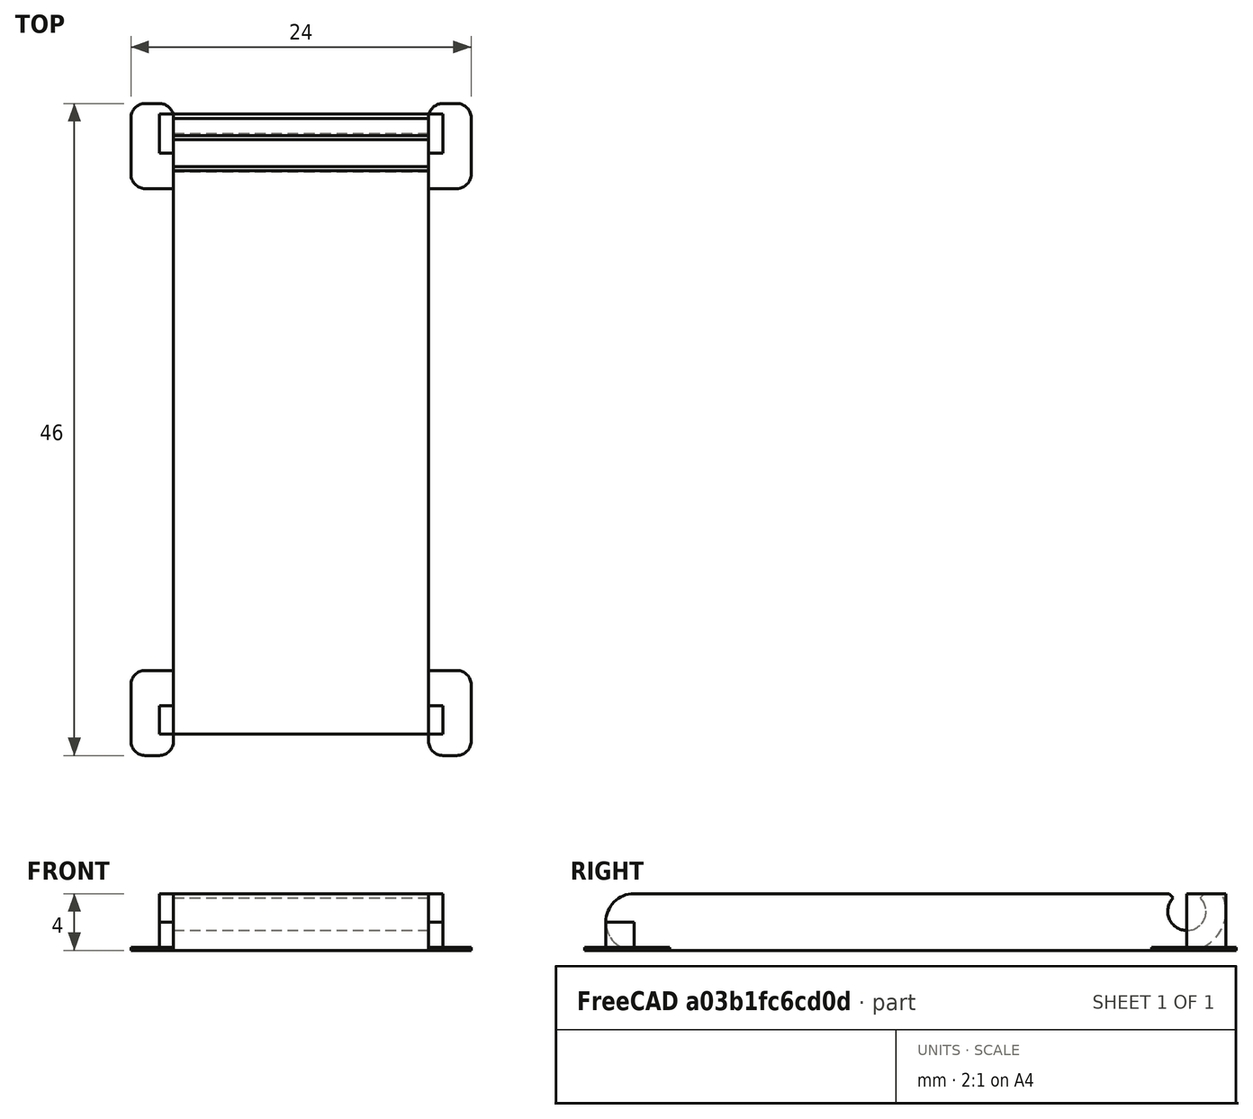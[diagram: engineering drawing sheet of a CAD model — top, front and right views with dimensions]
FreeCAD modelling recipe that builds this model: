
FCSTD DOCUMENT  (FreeCAD 0.14R3700 (Git))
Label: Phone_stand_flippable_backplate
License: CC-BY 3.0
LicenseURL: http://creativecommons.org/licenses/by/3.0/
objects: Sketcher::SketchObject×4, PartDesign::Pad×4, Mesh::Feature×1
note: 12 computed .brp shape members not serialized (recipe doc carries the construction recipe); baked Part::Feature solids carry a one-line shape summary decoded from their .brp

FEATURE [Sketcher::SketchObject] Sketch  label="X-Section"
  Placement = pos=(0,0,0) rot=(0.57735,0.57735,0.57735;2.0944rad)
  sketch-geometry (9):
    g0: LineSegment StartX=-1.308e-09 StartY=4 StartZ=0 EndX=37.7619 EndY=4 EndZ=0
    g1: LineSegment StartX=39 StartY=0 StartZ=0 EndX=0 EndY=0 EndZ=0
    g2: ArcOfCircle CenterX=1.7167e-08 CenterY=2 CenterZ=0 NormalX=0 NormalY=0 NormalZ=1 Radius=2 StartAngle=1.5708 EndAngle=4.71239
    g3: ArcOfCircle CenterX=39 CenterY=2.75 CenterZ=0 NormalX=0 NormalY=0 NormalZ=1 Radius=1.35 StartAngle=2.35139 EndAngle=7.07338
    g4: LineSegment StartX=37.7619 StartY=4 StartZ=0 EndX=38.05 EndY=3.70917 EndZ=0
    g5: LineSegment [constr] StartX=38.05 StartY=3.70917 StartZ=0 EndX=39.95 EndY=3.70917 EndZ=0
    g6: LineSegment StartX=39.95 StartY=3.70917 StartZ=0 EndX=40.2381 EndY=4 EndZ=0
    g7: ArcOfCircle CenterX=39 CenterY=2.75 CenterZ=0 NormalX=0 NormalY=0 NormalZ=1 Radius=2.75 StartAngle=4.71239 EndAngle=6.75505
    g8: LineSegment StartX=40.2381 StartY=4 StartZ=0 EndX=41.4495 EndY=4 EndZ=0
  constraints (27):
    c: Horizontal(g0)
    c: Horizontal(g1)
    c: Coincident(g2,g0)
    c: Coincident(g2,g1)
    c: Tangent(g2,g0)
    c: Tangent(g2,g1)
    c: Coincident(g1,g-1)
    c: Radius(g2) = 2
    c: Coincident(g4,g3)
    c: Coincident(g5,g3)
    c: Coincident(g5,g3)
    c: Horizontal(g5)
    c: Coincident(g6,g3)
    c: DistanceX(g3,g3) = 0.95
    c: PointOnObject(g3,g6)
    c: PointOnObject(g3,g4)
    c: DistanceX(g2,g3) = 39
    c: Coincident(g0,g4)
    c: Coincident(g8,g6)
    c: Horizontal(g8)
    c: Coincident(g8,g7)
    c: PointOnObject(g0,g8)
    c: Coincident(g7,g3)
    c: Coincident(g7,g1)
    c: Radius(g3) = 1.35
    c: DistanceY(g3,g1) = -2.75
    c: Tangent(g7,g1)
FEATURE [PartDesign::Pad] Pad
  Length = 18
  Length2 = 100
  Placement = pos=(0,0,0) rot=(0.57735,0.57735,0.57735;2.0944rad)
  Sketch = -> Sketch
  Type = 0
FEATURE [Sketcher::SketchObject] Sketch002  label="Brim"
  sketch-geometry (29):
    g0: LineSegment StartX=0 StartY=2.5 StartZ=0 EndX=0 EndY=-2.5 EndZ=0
    g1: LineSegment StartX=-1 StartY=-3.5 StartZ=0 EndX=-2 EndY=-3.5 EndZ=0
    g2: LineSegment StartX=-3 StartY=-2.5 StartZ=0 EndX=-3 EndY=1.5 EndZ=0
    g3: LineSegment StartX=-2 StartY=2.5 StartZ=0 EndX=0 EndY=2.5 EndZ=0
    g4: ArcOfCircle CenterX=-2 CenterY=1.5 CenterZ=0 NormalX=0 NormalY=0 NormalZ=1 Radius=1 StartAngle=1.5708 EndAngle=3.14159
    g5: ArcOfCircle CenterX=-2 CenterY=-2.5 CenterZ=0 NormalX=0 NormalY=0 NormalZ=1 Radius=1 StartAngle=3.14159 EndAngle=4.71239
    g6: ArcOfCircle CenterX=-1 CenterY=-2.5 CenterZ=0 NormalX=0 NormalY=0 NormalZ=1 Radius=1 StartAngle=4.71239 EndAngle=6.28319
    g7: LineSegment StartX=18 StartY=2.5 StartZ=0 EndX=20 EndY=2.5 EndZ=0
    g8: LineSegment StartX=21 StartY=1.5 StartZ=0 EndX=21 EndY=-2.5 EndZ=0
    g9: LineSegment StartX=20 StartY=-3.5 StartZ=0 EndX=19 EndY=-3.5 EndZ=0
    g10: LineSegment StartX=18 StartY=-2.5 StartZ=0 EndX=18 EndY=2.5 EndZ=0
    g11: ArcOfCircle CenterX=20 CenterY=1.5 CenterZ=0 NormalX=0 NormalY=0 NormalZ=1 Radius=1 StartAngle=0 EndAngle=1.5708
    g12: ArcOfCircle CenterX=20 CenterY=-2.5 CenterZ=0 NormalX=0 NormalY=0 NormalZ=1 Radius=1 StartAngle=4.71239 EndAngle=6.28319
    g13: ArcOfCircle CenterX=19 CenterY=-2.5 CenterZ=0 NormalX=0 NormalY=0 NormalZ=1 Radius=1 StartAngle=3.14159 EndAngle=4.71239
    g14: LineSegment StartX=19 StartY=42.5 StartZ=0 EndX=20 EndY=42.5 EndZ=0
    g15: LineSegment StartX=21 StartY=41.5 StartZ=0 EndX=21 EndY=37.5 EndZ=0
    g16: LineSegment StartX=20 StartY=36.5 StartZ=0 EndX=18 EndY=36.5 EndZ=0
    g17: LineSegment StartX=18 StartY=36.5 StartZ=0 EndX=18 EndY=41.5 EndZ=0
    g18: LineSegment StartX=-1 StartY=42.5 StartZ=0 EndX=-2 EndY=42.5 EndZ=0
    g19: LineSegment StartX=-3 StartY=41.5 StartZ=0 EndX=-3 EndY=37.5 EndZ=0
    g20: LineSegment StartX=-2 StartY=36.5 StartZ=0 EndX=0 EndY=36.5 EndZ=0
    g21: LineSegment StartX=0 StartY=36.5 StartZ=0 EndX=0 EndY=41.5 EndZ=0
    g22: ArcOfCircle CenterX=20 CenterY=37.5 CenterZ=0 NormalX=0 NormalY=0 NormalZ=1 Radius=1 StartAngle=4.71239 EndAngle=6.28319
    g23: ArcOfCircle CenterX=19 CenterY=41.5 CenterZ=0 NormalX=0 NormalY=0 NormalZ=1 Radius=1 StartAngle=1.5708 EndAngle=3.14159
    g24: ArcOfCircle CenterX=20 CenterY=41.5 CenterZ=0 NormalX=0 NormalY=0 NormalZ=1 Radius=1 StartAngle=0 EndAngle=1.5708
    g25: ArcOfCircle CenterX=-2 CenterY=41.5 CenterZ=0 NormalX=0 NormalY=0 NormalZ=1 Radius=1 StartAngle=1.5708 EndAngle=3.14159
    g26: ArcOfCircle CenterX=-1 CenterY=41.5 CenterZ=0 NormalX=0 NormalY=0 NormalZ=1 Radius=1 StartAngle=0 EndAngle=1.5708
    g27: ArcOfCircle CenterX=-2 CenterY=37.5 CenterZ=0 NormalX=0 NormalY=0 NormalZ=1 Radius=1 StartAngle=3.14159 EndAngle=4.71239
    g28: LineSegment [constr] StartX=0 StartY=39 StartZ=0 EndX=40 EndY=39 EndZ=0
  constraints (75):
    c: Vertical(g0)
    c: Horizontal(g1)
    c: Vertical(g2)
    c: Horizontal(g3)
    c: Tangent(g2,g4)
    c: Tangent(g3,g4)
    c: Tangent(g1,g5)
    c: Tangent(g2,g5)
    c: Coincident(g3,g0)
    c: Tangent(g0,g6)
    c: Tangent(g1,g6)
    c: Radius(g5) = 1
    c: Radius(g4) = 1
    c: Radius(g6) = 1
    c: DistanceX(g1) = -1
    c: Symmetric(g0,g0,g-1)
    c: DistanceY(g2) = 4
    c: Coincident(g10,g7)
    c: Horizontal(g7)
    c: Horizontal(g9)
    c: Vertical(g8)
    c: Vertical(g10)
    c: Tangent(g7,g11)
    c: Tangent(g8,g11)
    c: Tangent(g8,g12)
    c: Tangent(g9,g12)
    c: Tangent(g9,g13)
    c: Tangent(g10,g13)
    c: Radius(g13) = 1
    c: Radius(g12) = 1
    c: Radius(g11) = 1
    c: DistanceX(g9) = -1
    c: PointOnObject(g0,g7)
    c: DistanceX(g0,g10) = 18
    c: Equal(g2,g8)
    c: Coincident(g16,g17)
    c: Horizontal(g14)
    c: Horizontal(g16)
    c: Vertical(g15)
    c: Vertical(g17)
    c: Coincident(g20,g21)
    c: Horizontal(g18)
    c: Horizontal(g20)
    c: Vertical(g19)
    c: Vertical(g21)
    c: Tangent(g15,g22)
    c: Tangent(g16,g22)
    c: Tangent(g14,g23)
    c: Tangent(g17,g23)
    c: Tangent(g14,g24)
    c: Tangent(g15,g24)
    c: Tangent(g18,g25)
    c: Tangent(g19,g25)
    c: Tangent(g18,g26)
    c: Tangent(g21,g26)
    c: Tangent(g19,g27)
    c: Tangent(g20,g27)
    c: PointOnObject(g16,g10)
    c: PointOnObject(g20,g0)
    c: Radius(g25) = 1
    c: Radius(g27) = 1
    c: Radius(g24) = 1
    c: Radius(g23) = 1
    c: Radius(g22) = 1
    c: Equal(g3,g20)
    c: Equal(g16,g7)
    c: Equal(g19,g2)
    c: Equal(g15,g8)
    c: PointOnObject(g20,g16)
    c: Horizontal(g28)
    c: DistanceY(g-1,g28) = 39
    c: PointOnObject(g28,g-2)
    c: DistanceX(g28) = 40
    c: Symmetric(g17,g16,g28)
    c: Radius(g26) = 1
FEATURE [PartDesign::Pad] Pad002  label="Brim-Pad"
  Length = 0.2
  Length2 = 100
  Sketch = -> Sketch002
  Type = 0
FEATURE [Sketcher::SketchObject] Sketch003  label="Support1"
  sketch-geometry (8):
    g0: LineSegment StartX=18 StartY=0 StartZ=0 EndX=19 EndY=0 EndZ=0
    g1: LineSegment StartX=19 StartY=0 StartZ=0 EndX=19 EndY=-2 EndZ=0
    g2: LineSegment StartX=19 StartY=-2 StartZ=0 EndX=18 EndY=-2 EndZ=0
    g3: LineSegment StartX=18 StartY=-2 StartZ=0 EndX=18 EndY=0 EndZ=0
    g4: LineSegment StartX=-1 StartY=0 StartZ=0 EndX=0 EndY=0 EndZ=0
    g5: LineSegment StartX=0 StartY=0 StartZ=0 EndX=0 EndY=-2 EndZ=0
    g6: LineSegment StartX=0 StartY=-2 StartZ=0 EndX=-1 EndY=-2 EndZ=0
    g7: LineSegment StartX=-1 StartY=-2 StartZ=0 EndX=-1 EndY=0 EndZ=0
  constraints (23):
    c: Coincident(g0,g1)
    c: Coincident(g1,g2)
    c: Coincident(g2,g3)
    c: Coincident(g3,g0)
    c: Horizontal(g0)
    c: Horizontal(g2)
    c: Vertical(g1)
    c: Vertical(g3)
    c: Coincident(g4,g5)
    c: Coincident(g5,g6)
    c: Coincident(g6,g7)
    c: Coincident(g7,g4)
    c: Horizontal(g4)
    c: Horizontal(g6)
    c: Vertical(g5)
    c: Vertical(g7)
    c: Coincident(g4,g-1)
    c: DistanceY(g5) = -2
    c: PointOnObject(g0,g-1)
    c: DistanceX(g5,g2) = 18
    c: Equal(g5,g3)
    c: Equal(g4,g0)
    c: DistanceX(g6) = -1
FEATURE [PartDesign::Pad] Pad003  label="Support1-Pad"
  Length = 2
  Length2 = 100
  Sketch = -> Sketch003
  Type = 0
FEATURE [Sketcher::SketchObject] Sketch005  label="Support2"
  sketch-geometry (8):
    g0: LineSegment StartX=18 StartY=41.75 StartZ=0 EndX=19 EndY=41.75 EndZ=0
    g1: LineSegment StartX=19 StartY=41.75 StartZ=0 EndX=19 EndY=39 EndZ=0
    g2: LineSegment StartX=19 StartY=39 StartZ=0 EndX=18 EndY=39 EndZ=0
    g3: LineSegment StartX=18 StartY=39 StartZ=0 EndX=18 EndY=41.75 EndZ=0
    g4: LineSegment StartX=-1 StartY=41.75 StartZ=0 EndX=0 EndY=41.75 EndZ=0
    g5: LineSegment StartX=0 StartY=41.75 StartZ=0 EndX=0 EndY=39 EndZ=0
    g6: LineSegment StartX=0 StartY=39 StartZ=0 EndX=-1 EndY=39 EndZ=0
    g7: LineSegment StartX=-1 StartY=39 StartZ=0 EndX=-1 EndY=41.75 EndZ=0
  constraints (24):
    c: Coincident(g0,g1)
    c: Coincident(g1,g2)
    c: Coincident(g2,g3)
    c: Coincident(g3,g0)
    c: Horizontal(g0)
    c: Horizontal(g2)
    c: Vertical(g1)
    c: Vertical(g3)
    c: Coincident(g4,g5)
    c: Coincident(g5,g6)
    c: Coincident(g6,g7)
    c: Coincident(g7,g4)
    c: Horizontal(g4)
    c: Horizontal(g6)
    c: Vertical(g5)
    c: Vertical(g7)
    c: PointOnObject(g-1,g5)
    c: Equal(g7,g1)
    c: DistanceY(g1) = -2.75
    c: PointOnObject(g0,g4)
    c: DistanceY(g-1,g1) = 39
    c: DistanceX(g4,g0) = 18
    c: DistanceX(g2) = -1
    c: Equal(g2,g6)
FEATURE [PartDesign::Pad] Pad004  label="Support2-Pad"
  Length = 4
  Length2 = 100
  Sketch = -> Sketch005
  Type = 0
FEATURE [Mesh::Feature] Mesh  label="Pad (Meshed)"
